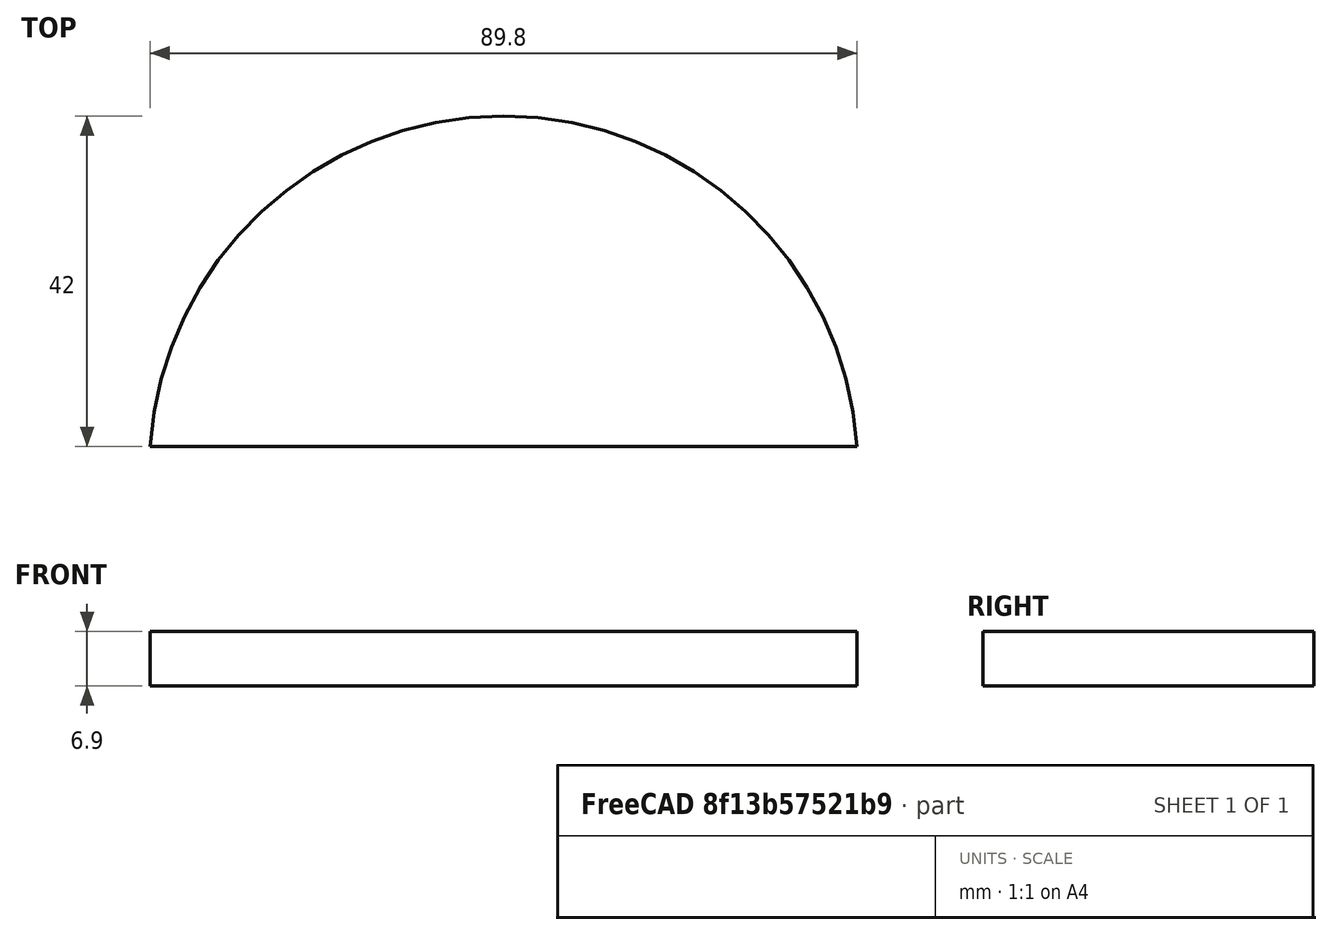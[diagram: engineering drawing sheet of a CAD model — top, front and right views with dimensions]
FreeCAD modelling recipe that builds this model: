
FCSTD DOCUMENT  (FreeCAD 1.0R39319 (Git))
Label: cylinder_90x6_with_1cuts
License: All rights reserved
LicenseURL: https://en.wikipedia.org/wiki/All_rights_reserved
objects: Sketcher::SketchObject×2, PartDesign::Pad×1, PartDesign::Pocket×1, PartDesign::Body×1
note: 11 computed .brp shape members not serialized (recipe doc carries the construction recipe); baked Part::Feature solids carry a one-line shape summary decoded from their .brp

FEATURE [Sketcher::SketchObject] Sketch_1
  ArcFitTolerance = 1e-06
  AttachmentSupport = -> [XY_Plane]
  FullyConstrained = false
  MakeInternals = false
  MapMode = 5
  sketch-geometry (1):
    g0: Circle CenterX=0 CenterY=0 CenterZ=0 NormalX=0 NormalY=0 NormalZ=1 AngleXU=0 Radius=45
FEATURE [PartDesign::Pad] Pad_1
  Direction = (0,0,1)
  Length = 6.9
  Length2 = 10
  Profile = -> Sketch_1
  Refine = true
  Suppressed = false
  Type = 0
FEATURE [Sketcher::SketchObject] Sketch_2
  ArcFitTolerance = 1e-06
  AttachmentSupport = -> [Pad_1]
  FullyConstrained = false
  MakeInternals = false
  MapMode = 5
  Placement = pos=(0,0,6.9) rot=(0,0,1;0rad)
  sketch-geometry (4):
    g0: LineSegment StartX=-45 StartY=-3 StartZ=0 EndX=45 EndY=-3 EndZ=0
    g1: LineSegment StartX=45 StartY=-3 StartZ=0 EndX=45 EndY=3 EndZ=0
    g2: LineSegment StartX=45 StartY=3 StartZ=0 EndX=-45 EndY=3 EndZ=0
    g3: LineSegment StartX=-45 StartY=3 StartZ=0 EndX=-45 EndY=-3 EndZ=0
  constraints (4):
    c: Coincident(g0,g1)
    c: Coincident(g1,g2)
    c: Coincident(g2,g3)
    c: Coincident(g3,g0)
FEATURE [PartDesign::Pocket] Pocket_2
  BaseFeature = -> Pad_1
  Direction = (0,0,-1)
  Length = 5
  Length2 = 5
  Profile = -> Sketch_2
  Refine = true
  Suppressed = false
  Type = 1
FEATURE [PartDesign::Body] Body
  AllowCompound = false
  Group = -> [Sketch_1,Pad_1,Sketch_2,Pocket_2]
  Origin = -> Origin
  Tip = -> Pocket_2
